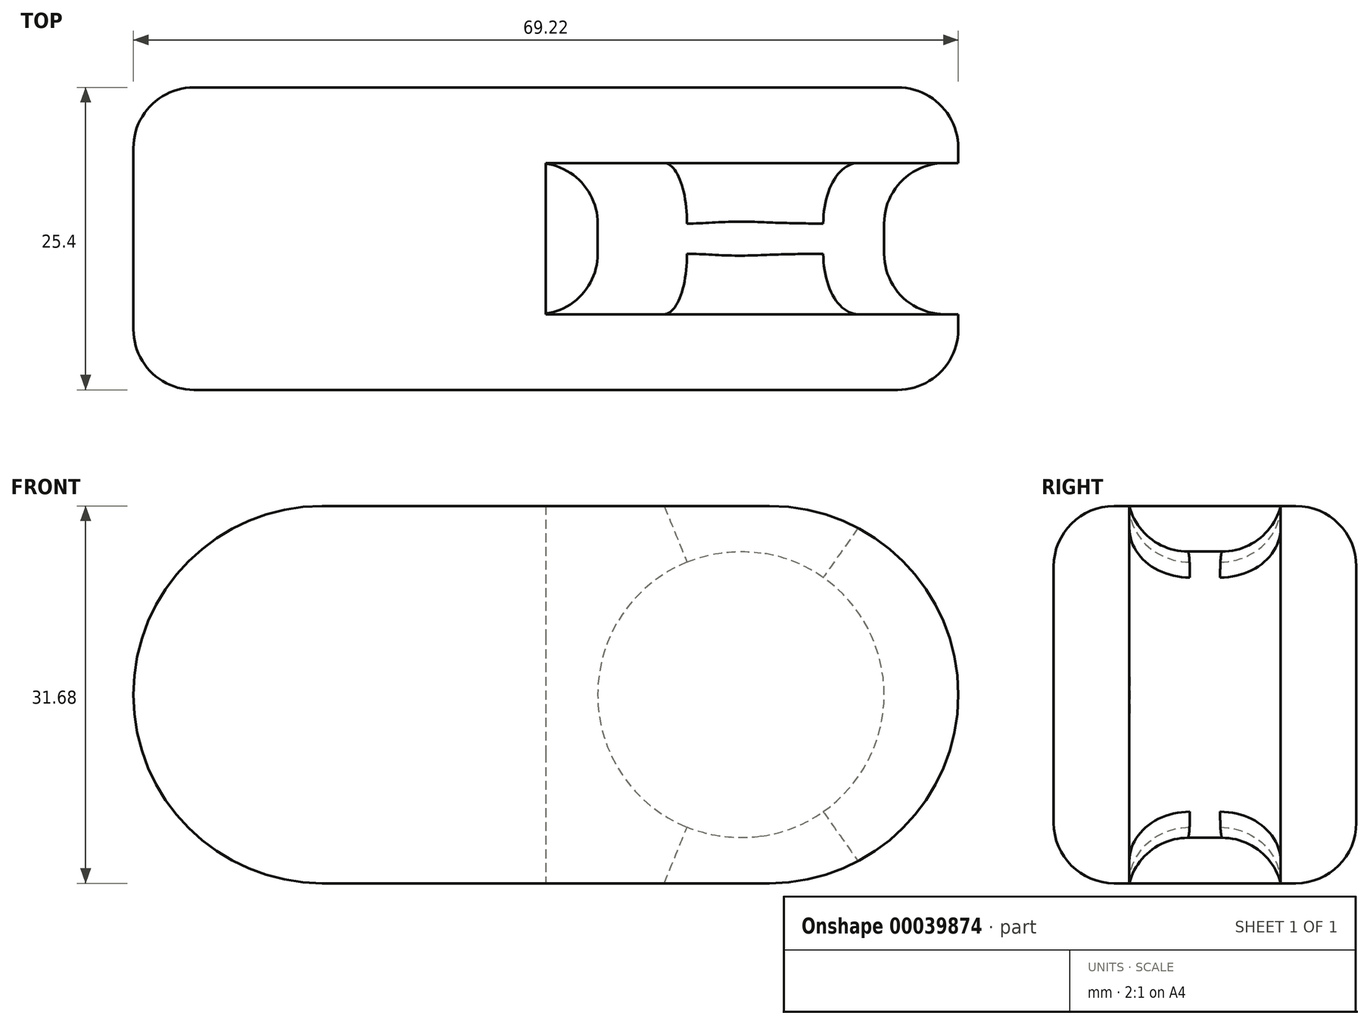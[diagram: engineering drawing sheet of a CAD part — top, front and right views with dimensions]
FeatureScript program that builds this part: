
annotation { "Feature Type Name" : "Feature", "Feature Type Description" : "" }
export const myFeature = defineFeature(function(context is Context, id is Id, definition is map)
    precondition{}
    {
        {
            var Q0;
            Q0=qCreatedBy(makeId("Front.planeOp"),FACE);
            var sketch = newSketch(context, id + "F0", { "sketchPlane" : qUnion([Q0])});
            skLineSegment(sketch, "E0", {"start": v(0, 15.84) * mm, "end": v(18.77, 15.84) * mm});
            skLineSegment(sketch, "E1.MirrorCS", {"start": v(0, -15.84) * mm, "end": v(18.77, -15.84) * mm});
            skArc(sketch, "E2", {"start": v(18.77, -15.84) * mm, "mid": v(34.6, 0) * mm, "end": v(18.77, 15.84) * mm});
            skArc(sketch, "E3.MirrorCS", {"start": v(-18.77, -15.84) * mm, "mid": v(-34.6, 0) * mm, "end": v(-18.77, 15.84) * mm});
            skLineSegment(sketch, "E4.MirrorCS", {"start": v(0, 15.84) * mm, "end": v(-18.77, 15.84) * mm});
            skLineSegment(sketch, "E5.MirrorCS", {"start": v(0, -15.84) * mm, "end": v(-18.77, -15.84) * mm});
            skSolve(sketch);
        }
        {
            var Q0;
            Q0=makeQuery(id+"F0.imprint","IMPRINT",FACE,{"disambiguationData":[TD([[makeQuery(id+"F0.imprint","IMPRINT",EDGE,{"derivedFrom":sQuery(id+"F0.wireOp",EDGE,"E0")}),-1.0]])]});
            extrude(context, id + "F1", {"entities" : qUnion([Q0]), "depth" : 12.7 * mm, "hasSecondDirection" : true, "secondDirectionOppositeDirection" : true, "secondDirectionDepth" : 12.7 * mm});
        }
        {
            var Q0;
            Q0=qCreatedBy(makeId("Front.planeOp"),FACE);
            var sketch = newSketch(context, id + "F2", { "sketchPlane" : qUnion([Q0])});
            skLineSegment(sketch, "E6", {"start": v(0, 16.6) * mm, "end": v(36.4, 16.6) * mm});
            skLineSegment(sketch, "E7.MirrorCS", {"start": v(0, -16.6) * mm, "end": v(36.4, -16.6) * mm});
            skArc(sketch, "E8", {"start": v(36.4, -16.6) * mm, "mid": v(53, 0) * mm, "end": v(36.4, 16.6) * mm});
            skLineSegment(sketch, "E9", {"start": v(0, 16.6) * mm, "end": v(0, -16.6) * mm});
            skCircle(sketch, "E10", {"center": v(16.37, 0) * mm, "radius": 12.02 * mm});
            skSolve(sketch);
        }
        {
            var Q0;
            Q0 = qSketchRegion(id + "F2", true);
            extrude(context, id + "F3", {"entities" : qUnion([Q0]), "operationType" : NewBodyOperationType.REMOVE, "depth" : 6.35 * mm, "hasSecondDirection" : true, "secondDirectionOppositeDirection" : true, "secondDirectionDepth" : 6.35 * mm});
        }
        {
            var Q0;
            Q0=makeQuery(id+"F1.opExtrude","CAP_FACE",FACE,{"disambiguationData":[OSD([sQuery(id+"F0.wireOp",EDGE,"E0"),sQuery(id+"F0.wireOp",EDGE,"E1.MirrorCS"),sQuery(id+"F0.wireOp",EDGE,"E2"),sQuery(id+"F0.wireOp",EDGE,"E3.MirrorCS"),sQuery(id+"F0.wireOp",EDGE,"E4.MirrorCS"),sQuery(id+"F0.wireOp",EDGE,"E5.MirrorCS")])],"isStart":false});
            var Q1;
            Q1=makeQuery(id+"F1.opExtrude","CAP_FACE",FACE,{"disambiguationData":[OSD([sQuery(id+"F0.wireOp",EDGE,"E0"),sQuery(id+"F0.wireOp",EDGE,"E1.MirrorCS"),sQuery(id+"F0.wireOp",EDGE,"E2"),sQuery(id+"F0.wireOp",EDGE,"E3.MirrorCS"),sQuery(id+"F0.wireOp",EDGE,"E4.MirrorCS"),sQuery(id+"F0.wireOp",EDGE,"E5.MirrorCS")])],"isStart":true});
            var Q2;
            Q2=makeQuery(id+"F3.boolean.opBoolean","COPY",FACE,{"derivedFrom":makeQuery(id+"F3.opExtrude","SWEPT_FACE",FACE,{"disambiguationData":[OSD([sQuery(id+"F2.wireOp",EDGE,"E10")])]})});
            fillet(context, id + "F4", {"entities" : qUnion([Q0, Q1, Q2]), "radius" : 5.08 * mm, "tangentPropagation" : true, "allowEdgeOverflow" : false});
        }
    });
